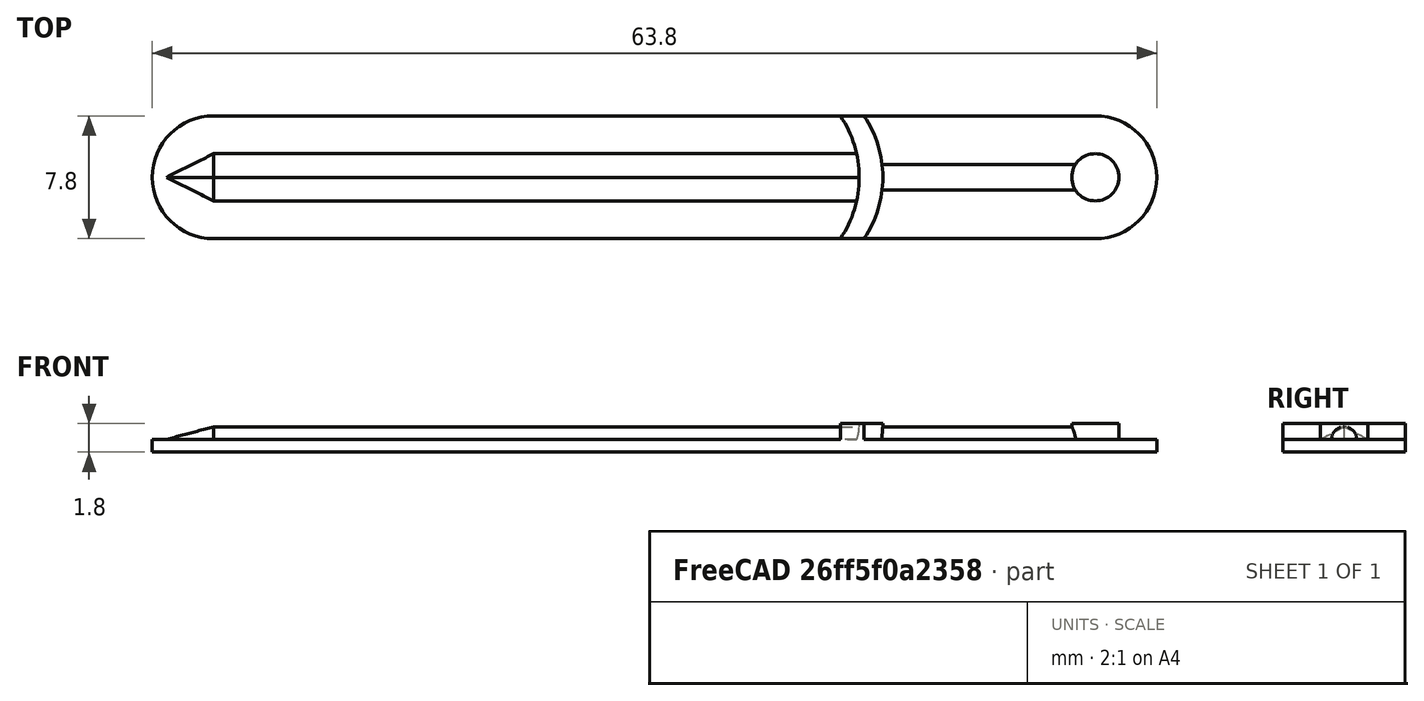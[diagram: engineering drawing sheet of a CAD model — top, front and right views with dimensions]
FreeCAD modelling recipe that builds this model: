
FCSTD DOCUMENT  (FreeCAD 1.0R38641 +678 (Git))
Label: SwordInset
License: All rights reserved
LicenseURL: https://en.wikipedia.org/wiki/All_rights_reserved
objects: Sketcher::SketchObject×7, PartDesign::Pad×5, PartDesign::AdditiveLoft×1, PartDesign::Plane×1, PartDesign::Mirrored×1, PartDesign::Body×1, Mesh::Feature×1
note: 36 computed .brp shape members not serialized (recipe doc carries the construction recipe); baked Part::Feature solids carry a one-line shape summary decoded from their .brp

FEATURE [Sketcher::SketchObject] Sketch
  ArcFitTolerance = 1e-06
  AttachmentSupport = -> [XY_Plane]
  FullyConstrained = true
  MakeInternals = false
  MapMode = 5
  sketch-geometry (4):
    g0: ArcOfCircle CenterX=0 CenterY=0 CenterZ=0 NormalX=0 NormalY=0 NormalZ=1 AngleXU=0 Radius=3.9 StartAngle=1.5708 EndAngle=4.71239
    g1: ArcOfCircle CenterX=56 CenterY=-2e-16 CenterZ=0 NormalX=0 NormalY=0 NormalZ=1 AngleXU=0 Radius=3.9 StartAngle=4.71239 EndAngle=7.85398
    g2: LineSegment StartX=0 StartY=3.9 StartZ=0 EndX=56 EndY=3.9 EndZ=0
    g3: LineSegment StartX=-7e-16 StartY=-3.9 StartZ=0 EndX=56 EndY=-3.9 EndZ=0
  constraints (9):
    c: Tangent(g0,g2) = 1.5708
    c: Tangent(g0,g3) = -1.5708
    c: Tangent(g1,g2) = 1.5708
    c: Tangent(g1,g3) = -1.5708
    c: Equal(g0,g1)
    c: Horizontal(g3)
    c: Coincident(g0,g-1)
    c: DistanceX(g0,g1) = 56
    c: Radius(g0) = 3.9
FEATURE [PartDesign::Pad] Pad
  Direction = (0,0,1)
  Length = 0.8
  Length2 = 10
  Profile = -> Sketch
  ReferenceAxis = -> Sketch [N_Axis]
  Refine = true
  Reversed = true
  Suppressed = false
  Type = 0
FEATURE [Sketcher::SketchObject] Sketch001
  ArcFitTolerance = 1e-06
  AttachmentSupport = -> [YZ_Plane]
  FullyConstrained = true
  MakeInternals = false
  MapMode = 5
  Placement = pos=(0,0,0) rot=(0.57735,0.57735,0.57735;2.0944rad)
  sketch-geometry (3):
    g0: LineSegment StartX=0 StartY=0 StartZ=0 EndX=1.5 EndY=0 EndZ=0
    g1: LineSegment StartX=1.5 StartY=0 StartZ=0 EndX=0 EndY=0.8 EndZ=0
    g2: LineSegment StartX=0 StartY=0.8 StartZ=0 EndX=0 EndY=0 EndZ=0
  constraints (8):
    c: Coincident(g0,g-1)
    c: PointOnObject(g0,g-1)
    c: Coincident(g1,g0)
    c: PointOnObject(g1,g-2)
    c: Coincident(g2,g1)
    c: Coincident(g2,g0)
    c: Distance(g2,g2) = 0.8
    c: DistanceX(g0,g0) = 1.5
FEATURE [Sketcher::SketchObject] Sketch002
  ArcFitTolerance = 1e-06
  AttachmentSupport = -> [Pad]
  FullyConstrained = true
  MakeInternals = false
  MapMode = 5
  sketch-geometry (1):
    g0: GeomPoint X=-3 Y=0 Z=0
  constraints (2):
    c: PointOnObject(g0,g-1)
    c: DistanceX(g0,g-1) = 3
FEATURE [PartDesign::AdditiveLoft] AdditiveLoft
  BaseFeature = -> Pad
  Closed = false
  Profile = -> Sketch001
  Refine = true
  Ruled = false
  Sections = -> [Sketch002]
  Suppressed = false
FEATURE [Sketcher::SketchObject] Sketch003
  ArcFitTolerance = 1e-06
  AttachmentSupport = -> [AdditiveLoft]
  FullyConstrained = true
  MakeInternals = false
  MapMode = 5
  sketch-geometry (2):
    g0: LineSegment StartX=54.5 StartY=2e-16 StartZ=0 EndX=57.5 EndY=0 EndZ=0
    g1: ArcOfCircle CenterX=56 CenterY=0 CenterZ=0 NormalX=0 NormalY=0 NormalZ=1 AngleXU=0 Radius=1.5 StartAngle=0 EndAngle=3.14159
  constraints (7):
    c: PointOnObject(g0,g-1)
    c: PointOnObject(g0,g-1)
    c: Coincident(g1,g0)
    c: Coincident(g1,g0)
    c: PointOnObject(g1,g0)
    c: DistanceX(g-1,g1) = 56
    c: Radius(g1) = 1.5
FEATURE [PartDesign::Pad] Pad001
  BaseFeature = -> AdditiveLoft
  Direction = (0,0,1)
  Length = 1
  Length2 = 10
  Profile = -> Sketch003
  ReferenceAxis = -> Sketch003 [N_Axis]
  Refine = true
  Suppressed = false
  Type = 0
FEATURE [PartDesign::Plane] DatumPlane
  AttachmentOffset = pos=(0,0,42) rot=(0,0,1;0rad)
  AttachmentSupport = -> [YZ_Plane]
  Length = 60
  MapMode = 5
  Placement = pos=(42,0,0) rot=(0.57735,0.57735,0.57735;2.0944rad)
  ResizeMode = 0
  Width = 60
FEATURE [Sketcher::SketchObject] Sketch004
  ArcFitTolerance = 1e-06
  AttachmentSupport = -> [DatumPlane]
  FullyConstrained = true
  MakeInternals = false
  MapMode = 5
  Placement = pos=(42,0,0) rot=(0.57735,0.57735,0.57735;2.0944rad)
  sketch-geometry (3):
    g0: LineSegment StartX=0 StartY=0 StartZ=0 EndX=0 EndY=0.8 EndZ=0
    g1: LineSegment StartX=0 StartY=0 StartZ=0 EndX=0.8 EndY=0 EndZ=0
    g2: ArcOfCircle CenterX=0 CenterY=0 CenterZ=0 NormalX=0 NormalY=0 NormalZ=1 AngleXU=0 Radius=0.8 StartAngle=0 EndAngle=1.5708
  constraints (8):
    c: Coincident(g0,g-1)
    c: PointOnObject(g0,g-2)
    c: Coincident(g1,g0)
    c: PointOnObject(g1,g-1)
    c: Coincident(g2,g0)
    c: Coincident(g2,g0)
    c: Coincident(g2,g1)
    c: Radius(g2) = 0.8
FEATURE [PartDesign::Pad] Pad002
  BaseFeature = -> Pad001
  Direction = (1,0,0)
  Length = 14
  Length2 = 10
  Profile = -> Sketch004
  ReferenceAxis = -> Sketch004 [N_Axis]
  Refine = true
  Suppressed = false
  Type = 0
FEATURE [Sketcher::SketchObject] Sketch005
  ArcFitTolerance = 1e-06
  AttachmentSupport = -> [Pad002]
  ExternalGeometry = -> [Pad002]
  FullyConstrained = true
  MakeInternals = false
  MapMode = 5
  sketch-geometry (4):
    g0: ArcOfCircle CenterX=34 CenterY=0 CenterZ=0 NormalX=0 NormalY=0 NormalZ=1 AngleXU=0 Radius=7 StartAngle=0 EndAngle=0.590941
    g1: ArcOfCircle CenterX=35.5 CenterY=0 CenterZ=0 NormalX=0 NormalY=0 NormalZ=1 AngleXU=0 Radius=7 StartAngle=0 EndAngle=0.590941
    g2: LineSegment StartX=41 StartY=0 StartZ=0 EndX=42.5 EndY=0 EndZ=0
    g3: LineSegment StartX=39.8129 StartY=3.9 StartZ=0 EndX=41.3129 EndY=3.9 EndZ=0
  constraints (14):
    c: PointOnObject(g0,g-1)
    c: PointOnObject(g1,g-1)
    c: PointOnObject(g0,g-1)
    c: PointOnObject(g1,g-1)
    c: Coincident(g2,g0)
    c: Coincident(g2,g1)
    c: DistanceX(g0,g1) = 1.5
    c: Coincident(g3,g0)
    c: Coincident(g3,g1)
    c: Horizontal(g3)
    c: PointOnObject(g0,g-3)
    c: DistanceX(g0,g1) = 1.5
    c: DistanceX(g0,g0) = 7
    c: DistanceX(g-1,g0) = 41
FEATURE [PartDesign::Pad] Pad003
  BaseFeature = -> Pad002
  Direction = (0,0,1)
  Length = 1
  Length2 = 10
  Profile = -> Sketch005
  ReferenceAxis = -> Sketch005 [N_Axis]
  Refine = true
  Suppressed = false
  Type = 0
FEATURE [Sketcher::SketchObject] Sketch007
  ArcFitTolerance = 1e-06
  AttachmentSupport = -> [Pad003]
  ExternalGeometry = -> [Pad003]
  FullyConstrained = true
  MakeInternals = false
  MapMode = 5
  Placement = pos=(0,0,0) rot=(0.57735,0.57735,0.57735;2.0944rad)
  sketch-geometry (3):
    g0: LineSegment StartX=0 StartY=0.8 StartZ=0 EndX=0 EndY=0 EndZ=0
    g1: LineSegment StartX=0 StartY=0 StartZ=0 EndX=1.5 EndY=0 EndZ=0
    g2: LineSegment StartX=1.5 StartY=0 StartZ=0 EndX=0 EndY=0.8 EndZ=0
  constraints (6):
    c: Coincident(g0,g-3)
    c: Coincident(g0,g-1)
    c: Coincident(g1,g0)
    c: Coincident(g1,g-3)
    c: Coincident(g2,g1)
    c: Coincident(g2,g0)
FEATURE [PartDesign::Pad] Pad004
  BaseFeature = -> Pad003
  Direction = (1,0,0)
  Length = 41
  Length2 = 10
  Profile = -> Sketch007
  ReferenceAxis = -> Sketch007 [N_Axis]
  Refine = true
  Suppressed = false
  Type = 0
FEATURE [PartDesign::Mirrored] Mirrored
  BaseFeature = -> Pad004
  MirrorPlane = -> Sketch001 [V_Axis]
  Originals = -> [AdditiveLoft,Pad001,Pad002,Pad003,Pad004]
  Refine = true
  Suppressed = false
  TransformMode = 0
FEATURE [PartDesign::Body] Body
  AllowCompound = false
  Group = -> [Sketch,Pad,Sketch001,Sketch002,AdditiveLoft,Sketch003,Pad001,DatumPlane,Sketch004,Pad002,Sketch005,Pad003,Sketch007,Pad004,Mirrored]
  Origin = -> Origin
  Tip = -> Mirrored
FEATURE [Mesh::Feature] Mesh  label="SwordInsert"
